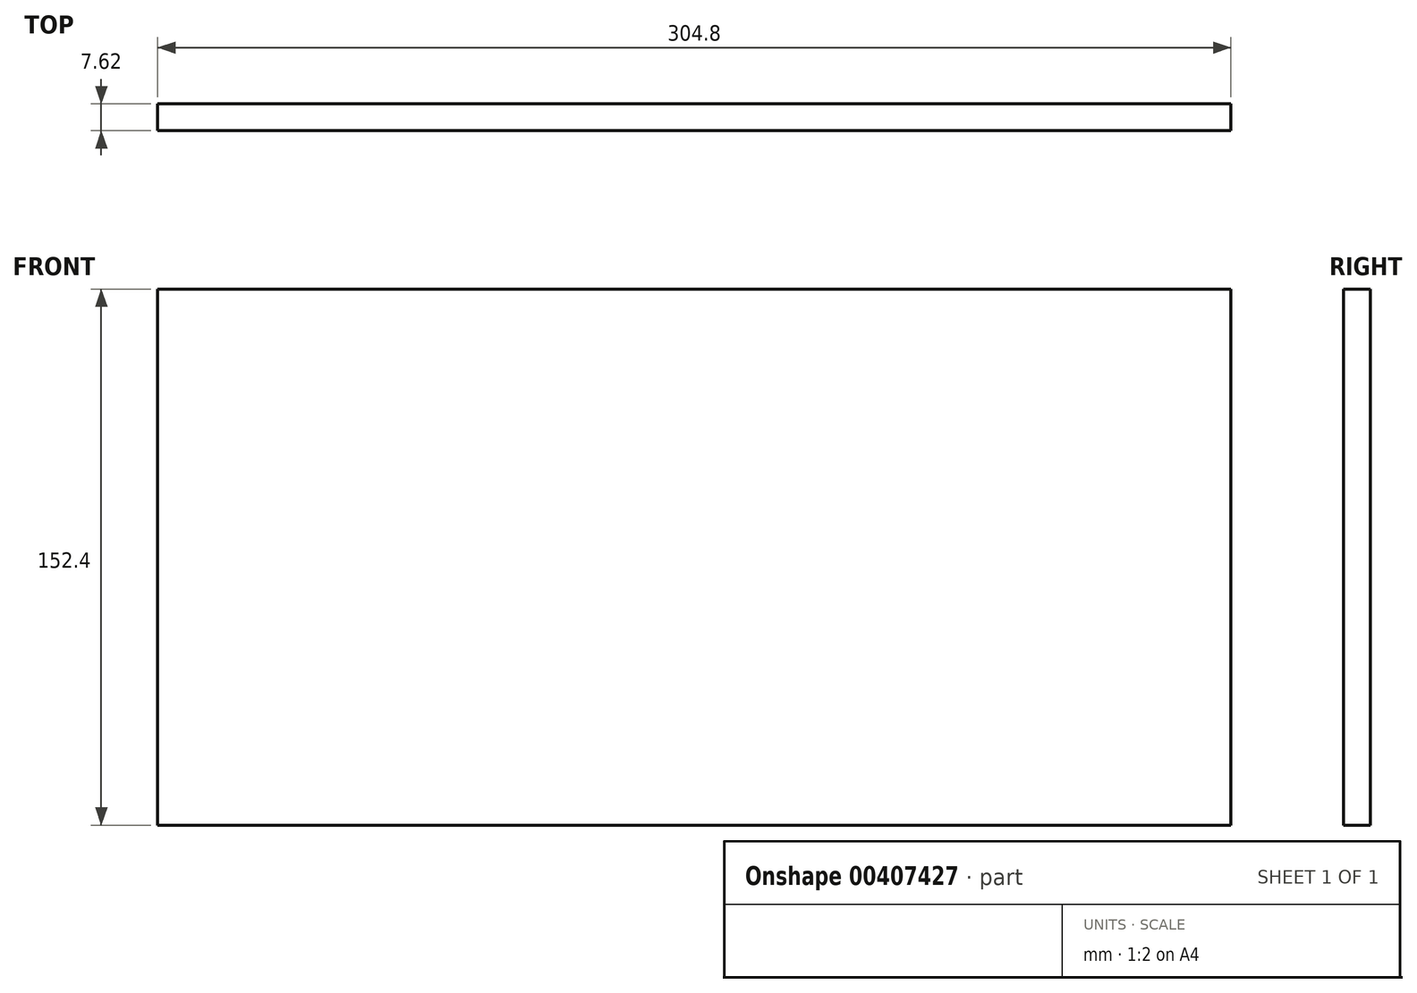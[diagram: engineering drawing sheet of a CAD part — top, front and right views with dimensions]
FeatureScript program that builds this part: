
annotation { "Feature Type Name" : "Feature", "Feature Type Description" : "" }
export const myFeature = defineFeature(function(context is Context, id is Id, definition is map)
    precondition{}
    {
        {
            var Q0;
            Q0=qCreatedBy(makeId("Front.planeOp"),FACE);
            var sketch = newSketch(context, id + "F0", { "sketchPlane" : qUnion([Q0])});
            skLineSegment(sketch, "E0.bottom", {"start": v(-144.39, 134.92) * mm, "end": v(160.41, 134.92) * mm});
            skLineSegment(sketch, "E0.top", {"start": v(-144.39, -17.48) * mm, "end": v(160.41, -17.48) * mm});
            skLineSegment(sketch, "E0.left", {"start": v(-144.39, 134.92) * mm, "end": v(-144.39, -17.48) * mm});
            skLineSegment(sketch, "E0.right", {"start": v(160.41, 134.92) * mm, "end": v(160.41, -17.48) * mm});
            skSolve(sketch);
        }
        {
            var Q0;
            Q0 = qSketchRegion(id + "F0", true);
            extrude(context, id + "F1", {"entities" : qUnion([Q0]), "depth" : 7.62 * mm});
        }
    });
